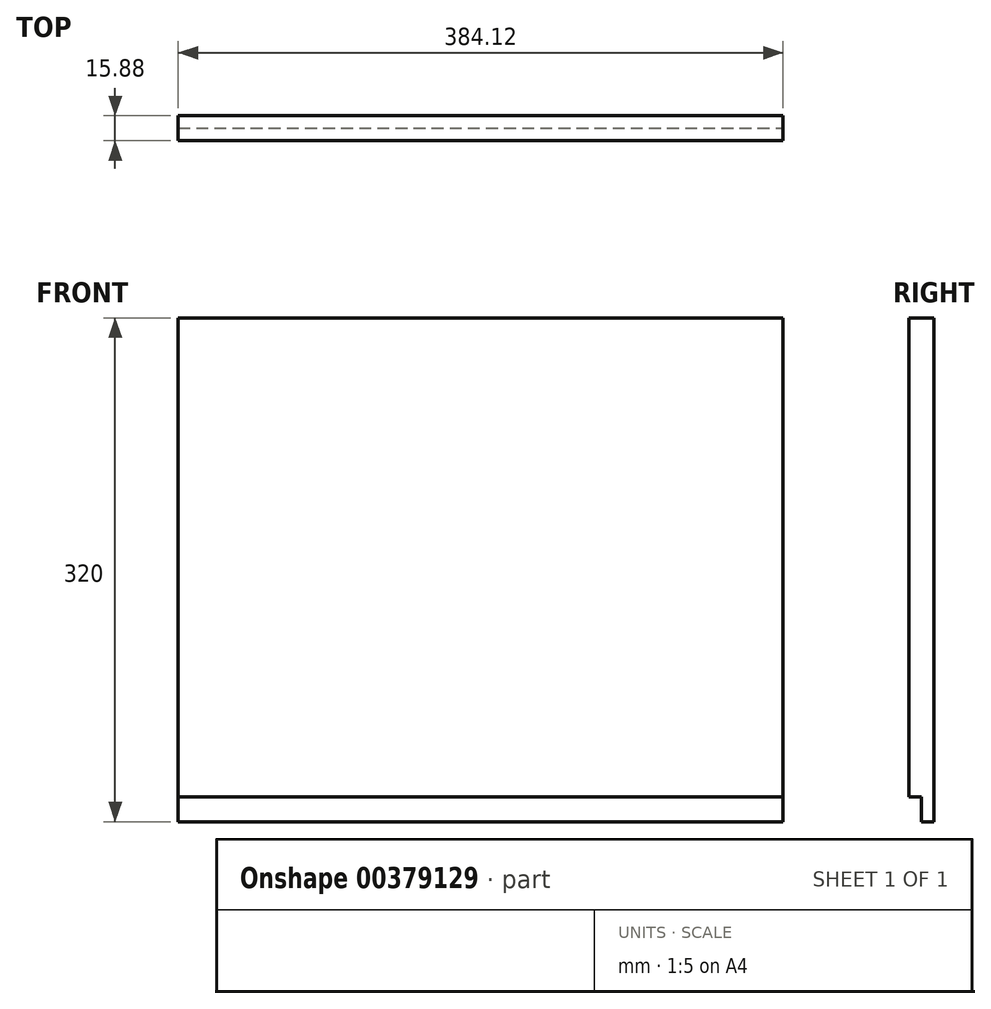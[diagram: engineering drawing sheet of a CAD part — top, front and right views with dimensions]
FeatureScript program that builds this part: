
annotation { "Feature Type Name" : "Feature", "Feature Type Description" : "" }
export const myFeature = defineFeature(function(context is Context, id is Id, definition is map)
    precondition{}
    {
        {
            var Q0;
            Q0=qCreatedBy(makeId("Front.planeOp"),FACE);
            var sketch = newSketch(context, id + "F0", { "sketchPlane" : qUnion([Q0])});
            skLineSegment(sketch, "E0.bottom", {"start": v(202.1, -146.2) * mm, "end": v(-182.02, -146.2) * mm});
            skLineSegment(sketch, "E0.top", {"start": v(202.1, 173.8) * mm, "end": v(-182.02, 173.8) * mm});
            skLineSegment(sketch, "E0.left", {"start": v(202.1, -146.2) * mm, "end": v(202.1, 173.8) * mm});
            skLineSegment(sketch, "E0.right", {"start": v(-182.02, -146.2) * mm, "end": v(-182.02, 173.8) * mm});
            skPoint(sketch, "E0.middle", {"position": v(10.04, 13.8) * mm});
            skSolve(sketch);
        }
        {
            var Q0;
            Q0=makeQuery(id+"F0.imprint","IMPRINT",FACE,{"disambiguationData":[TD([[makeQuery(id+"F0.imprint","IMPRINT",EDGE,{"derivedFrom":sQuery(id+"F0.wireOp",EDGE,"E0.bottom")}),-1.0]])]});
            extrude(context, id + "F1", {"entities" : qUnion([Q0]), "depth" : 15.88 * mm});
        }
        {
            var Q0;
            Q0=makeQuery(id+"F1.opExtrude","SWEPT_FACE",FACE,{"disambiguationData":[OSD([sQuery(id+"F0.wireOp",EDGE,"E0.left")])]});
            var sketch = newSketch(context, id + "F2", { "sketchPlane" : qUnion([Q0])});
            skLineSegment(sketch, "E1.bottom", {"start": v(-15.88, -146.2) * mm, "end": v(-7.94, -146.2) * mm});
            skLineSegment(sketch, "E1.top", {"start": v(-15.88, -130.32) * mm, "end": v(-7.94, -130.32) * mm});
            skLineSegment(sketch, "E1.left", {"start": v(-15.88, -146.2) * mm, "end": v(-15.88, -130.32) * mm});
            skLineSegment(sketch, "E1.right", {"start": v(-7.94, -146.2) * mm, "end": v(-7.94, -130.32) * mm});
            skSolve(sketch);
        }
        {
            var Q0;
            Q0=makeQuery(id+"F2.imprint","IMPRINT",FACE,{"disambiguationData":[TD([[makeQuery(id+"F2.imprint","IMPRINT",EDGE,{"derivedFrom":sQuery(id+"F2.wireOp",EDGE,"E1.bottom")}),1.0]])]});
            extrude(context, id + "F3", {"entities" : qUnion([Q0]), "operationType" : NewBodyOperationType.REMOVE, "endBound" : BoundingType.THROUGH_ALL, "oppositeDirection" : true, "depth" : 25 * mm});
        }
    });
